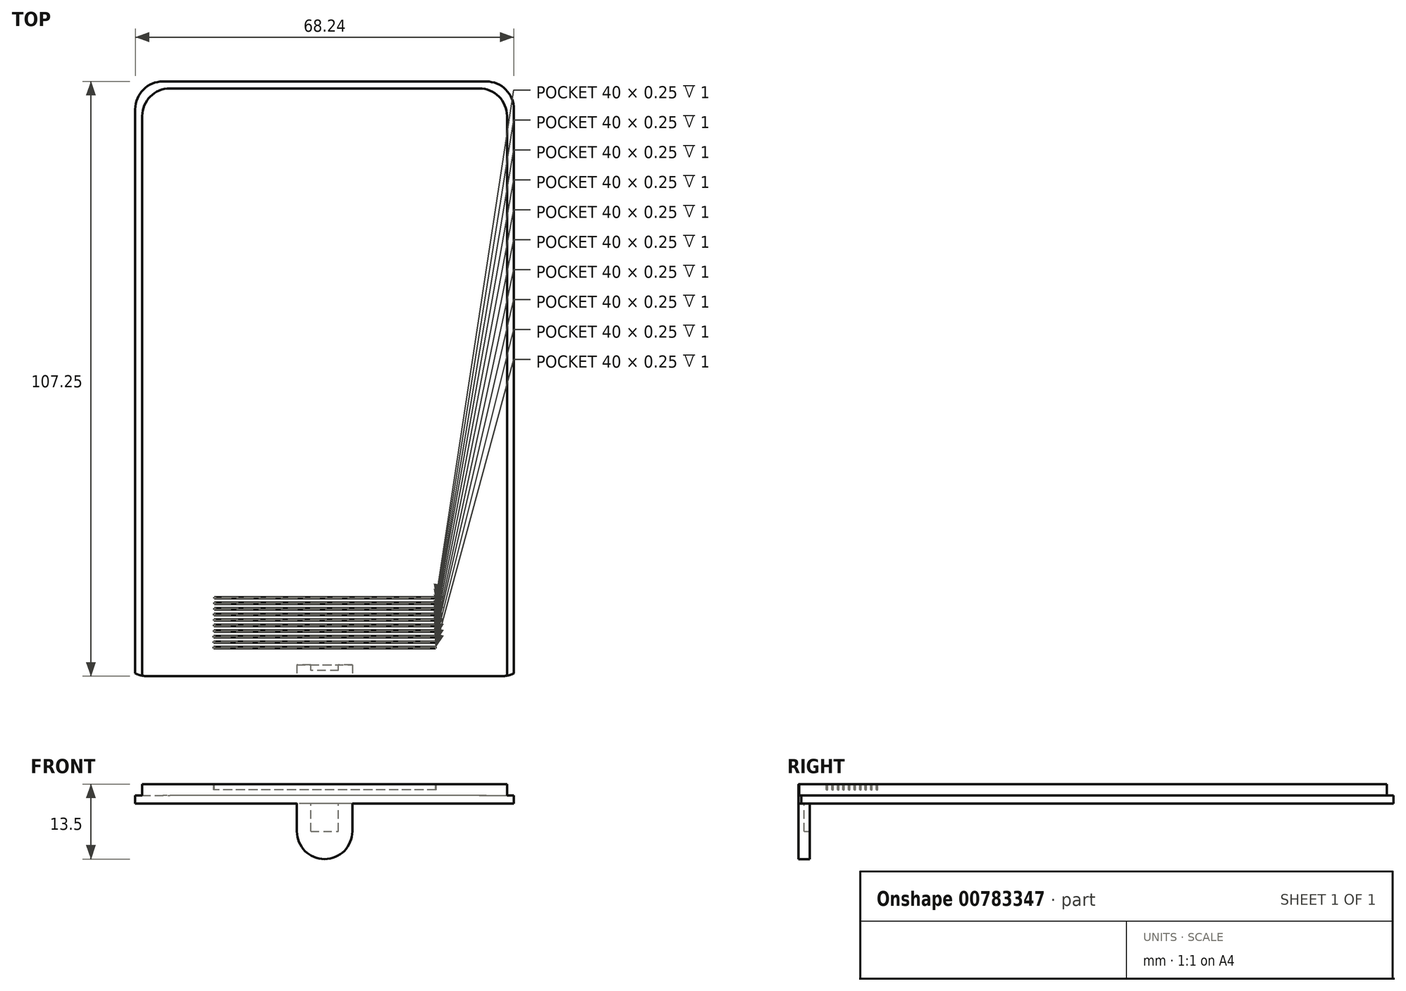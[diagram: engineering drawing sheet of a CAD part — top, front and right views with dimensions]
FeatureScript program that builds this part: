
annotation { "Feature Type Name" : "Feature", "Feature Type Description" : "" }
export const myFeature = defineFeature(function(context is Context, id is Id, definition is map)
    precondition{}
    {
        {
            var Q0;
            Q0=qCreatedBy(makeId("Front.planeOp"),FACE);
            var sketch = newSketch(context, id + "F0", { "sketchPlane" : qUnion([Q0])});
            skLineSegment(sketch, "E0.top", {"start": v(32.88, 3.5) * mm, "end": v(-32.87, 3.5) * mm});
            skLineSegment(sketch, "E0.left", {"start": v(32.88, 1.5) * mm, "end": v(32.88, 3.5) * mm});
            skLineSegment(sketch, "E0.right", {"start": v(-32.87, 1.5) * mm, "end": v(-32.87, 3.5) * mm});
            skLineSegment(sketch, "E1.bottom", {"start": v(34.12, 0) * mm, "end": v(-34.12, 0) * mm});
            skLineSegment(sketch, "E1.left", {"start": v(34.13, 0) * mm, "end": v(34.13, 1.5) * mm});
            skLineSegment(sketch, "E1.right", {"start": v(-34.12, 0) * mm, "end": v(-34.12, 1.5) * mm});
            skLineSegment(sketch, "E2", {"start": v(0, 3.25) * mm, "end": v(0, 44.31) * mm, "construction": true});
            skLineSegment(sketch, "E3", {"start": v(-34.12, 1.5) * mm, "end": v(-32.87, 1.5) * mm});
            skLineSegment(sketch, "E4", {"start": v(32.88, 1.5) * mm, "end": v(34.13, 1.5) * mm});
            skSolve(sketch);
        }
        {
            var Q0;
            Q0=makeQuery(id+"F0.imprint","IMPRINT",FACE,{"disambiguationData":[TD([[makeQuery(id+"F0.imprint","IMPRINT",EDGE,{"derivedFrom":sQuery(id+"F0.wireOp",EDGE,"E0.top")}),1.0]])]});
            extrude(context, id + "F1", {"entities" : qUnion([Q0]), "oppositeDirection" : true, "depth" : 106 * mm, "offsetDistance" : 25 * mm});
        }
        {
            var Q0;
            Q0=makeQuery(id+"F1.opExtrude","CAP_FACE",FACE,{"disambiguationData":[OSD([sQuery(id+"F0.wireOp",EDGE,"E0.top"),sQuery(id+"F0.wireOp",EDGE,"E0.left"),sQuery(id+"F0.wireOp",EDGE,"E0.right"),sQuery(id+"F0.wireOp",EDGE,"E1.bottom"),sQuery(id+"F0.wireOp",EDGE,"E1.left"),sQuery(id+"F0.wireOp",EDGE,"E1.right"),sQuery(id+"F0.wireOp",EDGE,"E3"),sQuery(id+"F0.wireOp",EDGE,"E4")])],"isStart":false});
            var sketch = newSketch(context, id + "F2", { "sketchPlane" : qUnion([Q0])});
            skLineSegment(sketch, "E5.bottom", {"start": v(-34.13, 1.5) * mm, "end": v(34.12, 1.5) * mm});
            skLineSegment(sketch, "E5.top", {"start": v(-34.13, 0) * mm, "end": v(34.12, 0) * mm});
            skLineSegment(sketch, "E5.left", {"start": v(-34.13, 1.5) * mm, "end": v(-34.13, 0) * mm});
            skLineSegment(sketch, "E5.right", {"start": v(34.12, 1.5) * mm, "end": v(34.12, 0) * mm});
            skSolve(sketch);
        }
        {
            var Q0;
            Q0 = qSketchRegion(id + "F2", true);
            extrude(context, id + "F3", {"entities" : qUnion([Q0]), "operationType" : NewBodyOperationType.ADD, "depth" : 1.25 * mm, "offsetDistance" : 25 * mm});
        }
        {
            var Q0;
            Q0=makeQuery(id+"F3.opExtrude","CAP_EDGE",EDGE,{"disambiguationData":[OSD([sQuery(id+"F2.wireOp",EDGE,"E5.left")])],"isStart":false});
            var Q1;
            Q1=makeQuery(id+"F3.opExtrude","CAP_EDGE",EDGE,{"disambiguationData":[OSD([sQuery(id+"F2.wireOp",EDGE,"E5.right")])],"isStart":false});
            var Q2;
            Q2=makeQuery(id+"F1.opExtrude","CAP_EDGE",EDGE,{"disambiguationData":[OSD([sQuery(id+"F0.wireOp",EDGE,"E0.right")])],"isStart":false});
            var Q3;
            Q3=makeQuery(id+"F1.opExtrude","CAP_EDGE",EDGE,{"disambiguationData":[OSD([sQuery(id+"F0.wireOp",EDGE,"E0.left")])],"isStart":false});
            fillet(context, id + "F4", {"entities" : qUnion([Q0, Q1, Q2, Q3]), "radius" : 5 * mm, "tangentPropagation" : true, "allowEdgeOverflow" : false});
        }
        {
            var Q0;
            Q0=qCreatedBy(makeId("Top.planeOp"),FACE);
            var sketch = newSketch(context, id + "F5", { "sketchPlane" : qUnion([Q0])});
            skLineSegment(sketch, "E6.0.0", {"start": v(-34.12, 73) * mm, "end": v(34.12, 73) * mm, "construction": true});
            skLineSegment(sketch, "E6.0.1", {"start": v(34.12, 73) * mm, "end": v(34.12, 5) * mm, "construction": true});
            skLineSegment(sketch, "E6.0.2", {"start": v(29.12, 0) * mm, "end": v(-29.12, 0) * mm, "construction": true});
            skLineSegment(sketch, "E6.0.3", {"start": v(-34.12, 5) * mm, "end": v(-34.12, 73) * mm, "construction": true});
            skPoint(sketch, "E7.middle", {"position": v(-2.88, 36.5) * mm});
            skPoint(sketch, "E8.visualSharp", {"position": v(-37, 0) * mm});
            skArc(sketch, "E8.filletArc", {"start": v(-37, 5) * mm, "mid": v(-35.54, 1.46) * mm, "end": v(-32, 0) * mm, "construction": true});
            skPoint(sketch, "E9.visualSharp", {"position": v(37, 0) * mm});
            skArc(sketch, "E9.filletArc", {"start": v(32, 0) * mm, "mid": v(35.54, 1.46) * mm, "end": v(37, 5) * mm, "construction": true});
            skArc(sketch, "E10", {"start": v(-37, 5) * mm, "mid": v(-35.54, 1.46) * mm, "end": v(-32, 0) * mm});
            skLineSegment(sketch, "E11", {"start": v(-32.48, -8.24) * mm, "end": v(-32, 0) * mm});
            skLineSegment(sketch, "E12", {"start": v(-37, 5) * mm, "end": v(-47.45, 5.13) * mm});
            skLineSegment(sketch, "E13", {"start": v(0, 0) * mm, "end": v(0, 9.43) * mm, "construction": true});
            skLineSegment(sketch, "E14.MirrorCS", {"start": v(37, 5) * mm, "end": v(47.87, 4.85) * mm});
            skLineSegment(sketch, "E15.MirrorCS", {"start": v(31.7, -9.05) * mm, "end": v(32, 0) * mm});
            skPoint(sketch, "E16.MirrorP", {"position": v(31.25, 0) * mm});
            skLineSegment(sketch, "E17", {"start": v(-47.45, 5.13) * mm, "end": v(-32.48, -8.24) * mm});
            skLineSegment(sketch, "E18", {"start": v(31.7, -9.05) * mm, "end": v(47.87, 4.85) * mm});
            skArc(sketch, "E19.MirrorCS", {"start": v(37, 5) * mm, "mid": v(35.54, 1.46) * mm, "end": v(32, 0) * mm});
            skArc(sketch, "E20.MirrorCS", {"start": v(37, 5) * mm, "mid": v(35.54, 1.46) * mm, "end": v(32, 0) * mm, "construction": true});
            skSolve(sketch);
        }
        {
            var Q0;
            Q0 = qSketchRegion(id + "F5", true);
            extrude(context, id + "F6", {"entities" : qUnion([Q0]), "operationType" : NewBodyOperationType.REMOVE, "depth" : 25 * mm, "offsetDistance" : 25 * mm});
        }
        {
            var Q0;
            Q0=makeQuery(id+"F1.opExtrude","CAP_FACE",FACE,{"disambiguationData":[OSD([sQuery(id+"F0.wireOp",EDGE,"E0.top"),sQuery(id+"F0.wireOp",EDGE,"E0.left"),sQuery(id+"F0.wireOp",EDGE,"E0.right"),sQuery(id+"F0.wireOp",EDGE,"E1.bottom"),sQuery(id+"F0.wireOp",EDGE,"E1.left"),sQuery(id+"F0.wireOp",EDGE,"E1.right"),sQuery(id+"F0.wireOp",EDGE,"E3"),sQuery(id+"F0.wireOp",EDGE,"E4")])],"isStart":true});
            var sketch = newSketch(context, id + "F7", { "sketchPlane" : qUnion([Q0])});
            skLineSegment(sketch, "E21.bottom", {"start": v(5, -10) * mm, "end": v(-5, -10) * mm});
            skLineSegment(sketch, "E21.top", {"start": v(5, 0) * mm, "end": v(-5, 0) * mm});
            skLineSegment(sketch, "E21.left", {"start": v(5, -10) * mm, "end": v(5, 0) * mm});
            skLineSegment(sketch, "E21.right", {"start": v(-5, -10) * mm, "end": v(-5, 0) * mm});
            skPoint(sketch, "E21.middle", {"position": v(0, -5) * mm});
            skSolve(sketch);
        }
        {
            var Q0;
            Q0 = qSketchRegion(id + "F7", true);
            extrude(context, id + "F8", {"entities" : qUnion([Q0]), "operationType" : NewBodyOperationType.ADD, "oppositeDirection" : true, "depth" : 2 * mm, "offsetDistance" : 25 * mm});
        }
        {
            var Q0;
            Q0=makeQuery(id+"F8.opExtrude","SWEPT_EDGE",EDGE,{"disambiguationData":[OSD([sQuery(id+"F0.wireOp",EDGE,"E1.bottom"),sQuery(id+"F7.wireOp",EDGE,"E21.top"),sQuery(id+"F7.wireOp",EDGE,"E21.left")])]});
            var Q1;
            Q1=makeQuery(id+"F8.opExtrude","SWEPT_EDGE",EDGE,{"disambiguationData":[OSD([sQuery(id+"F0.wireOp",EDGE,"E1.bottom"),sQuery(id+"F7.wireOp",EDGE,"E21.top"),sQuery(id+"F7.wireOp",EDGE,"E21.right")])]});
            var Q2;
            Q2=makeQuery(id+"F8.opExtrude","SWEPT_EDGE",EDGE,{"disambiguationData":[OSD([sQuery(id+"F7.wireOp",EDGE,"E21.bottom"),sQuery(id+"F7.wireOp",EDGE,"E21.right")])]});
            var Q3;
            Q3=makeQuery(id+"F8.opExtrude","SWEPT_EDGE",EDGE,{"disambiguationData":[OSD([sQuery(id+"F7.wireOp",EDGE,"E21.bottom"),sQuery(id+"F7.wireOp",EDGE,"E21.left")])]});
            fillet(context, id + "F9", {"entities" : qUnion([Q0, Q1, Q2, Q3]), "radius" : 5 * mm, "tangentPropagation" : true, "allowEdgeOverflow" : false});
        }
        {
            var Q0;
            Q0=makeQuery(id+"F8.opExtrude","CAP_FACE",FACE,{"disambiguationData":[OSD([sQuery(id+"F7.wireOp",EDGE,"E21.bottom"),sQuery(id+"F7.wireOp",EDGE,"E21.top"),sQuery(id+"F7.wireOp",EDGE,"E21.left"),sQuery(id+"F7.wireOp",EDGE,"E21.right")])],"isStart":false});
            var sketch = newSketch(context, id + "F10", { "sketchPlane" : qUnion([Q0])});
            skLineSegment(sketch, "E22.bottom", {"start": v(2.5, -5) * mm, "end": v(-2.5, -5) * mm});
            skLineSegment(sketch, "E22.top", {"start": v(2.5, 0) * mm, "end": v(-2.5, 0) * mm});
            skLineSegment(sketch, "E22.left", {"start": v(2.5, -5) * mm, "end": v(2.5, 0) * mm});
            skLineSegment(sketch, "E22.right", {"start": v(-2.5, -5) * mm, "end": v(-2.5, 0) * mm});
            skPoint(sketch, "E22.middle", {"position": v(0, -2.5) * mm});
            skPoint(sketch, "E23", {"position": v(0, 0) * mm});
            skSolve(sketch);
        }
        {
            var Q0;
            Q0 = qSketchRegion(id + "F10", true);
            extrude(context, id + "F11", {"entities" : qUnion([Q0]), "operationType" : NewBodyOperationType.REMOVE, "oppositeDirection" : true, "depth" : 1 * mm, "offsetDistance" : 25 * mm});
        }
        {
            var Q0;
            Q0=makeQuery(id+"F1.opExtrude","SWEPT_FACE",FACE,{"disambiguationData":[OSD([sQuery(id+"F0.wireOp",EDGE,"E0.top")])]});
            var sketch = newSketch(context, id + "F12", { "sketchPlane" : qUnion([Q0])});
            skLineSegment(sketch, "E24.bottom", {"start": v(20, 5) * mm, "end": v(-20, 5) * mm});
            skLineSegment(sketch, "E24.top", {"start": v(20, 5.25) * mm, "end": v(-20, 5.25) * mm});
            skLineSegment(sketch, "E24.left", {"start": v(20, 5) * mm, "end": v(20, 5.25) * mm});
            skLineSegment(sketch, "E24.right", {"start": v(-20, 5) * mm, "end": v(-20, 5.25) * mm});
            skPoint(sketch, "E24.middle", {"position": v(0, 5.13) * mm});
            skLineSegment(sketch, "E25", {"start": v(0, 0) * mm, "end": v(0, 5) * mm, "construction": true});
            skPoint(sketch, "E26.0.1.0", {"position": v(0.02, 6.12) * mm});
            skLineSegment(sketch, "E26.0.1.1", {"start": v(20.02, 6.25) * mm, "end": v(-19.98, 6.25) * mm});
            skLineSegment(sketch, "E26.0.1.2", {"start": v(20.02, 6) * mm, "end": v(-19.98, 6) * mm});
            skLineSegment(sketch, "E26.0.1.3", {"start": v(20.02, 6) * mm, "end": v(20.02, 6.25) * mm});
            skLineSegment(sketch, "E26.0.1.4", {"start": v(-19.98, 6) * mm, "end": v(-19.98, 6.25) * mm});
            skPoint(sketch, "E26.0.2.0", {"position": v(0.03, 7.12) * mm});
            skLineSegment(sketch, "E26.0.2.1", {"start": v(20.03, 7.25) * mm, "end": v(-19.97, 7.25) * mm});
            skLineSegment(sketch, "E26.0.2.2", {"start": v(20.03, 7) * mm, "end": v(-19.97, 7) * mm});
            skLineSegment(sketch, "E26.0.2.3", {"start": v(20.03, 7) * mm, "end": v(20.03, 7.25) * mm});
            skLineSegment(sketch, "E26.0.2.4", {"start": v(-19.97, 7) * mm, "end": v(-19.97, 7.25) * mm});
            skPoint(sketch, "E26.0.3.0", {"position": v(0.05, 8.12) * mm});
            skLineSegment(sketch, "E26.0.3.1", {"start": v(20.05, 8.25) * mm, "end": v(-19.95, 8.25) * mm});
            skLineSegment(sketch, "E26.0.3.2", {"start": v(20.05, 8) * mm, "end": v(-19.95, 8) * mm});
            skLineSegment(sketch, "E26.0.3.3", {"start": v(20.05, 8) * mm, "end": v(20.05, 8.25) * mm});
            skLineSegment(sketch, "E26.0.3.4", {"start": v(-19.95, 8) * mm, "end": v(-19.95, 8.25) * mm});
            skPoint(sketch, "E26.0.4.0", {"position": v(0.07, 9.12) * mm});
            skLineSegment(sketch, "E26.0.4.1", {"start": v(20.07, 9.25) * mm, "end": v(-19.93, 9.25) * mm});
            skLineSegment(sketch, "E26.0.4.2", {"start": v(20.07, 9) * mm, "end": v(-19.93, 9) * mm});
            skLineSegment(sketch, "E26.0.4.3", {"start": v(20.07, 9) * mm, "end": v(20.07, 9.25) * mm});
            skLineSegment(sketch, "E26.0.4.4", {"start": v(-19.93, 9) * mm, "end": v(-19.93, 9.25) * mm});
            skPoint(sketch, "E26.0.5.0", {"position": v(0.08, 10.12) * mm});
            skLineSegment(sketch, "E26.0.5.1", {"start": v(20.08, 10.25) * mm, "end": v(-19.92, 10.25) * mm});
            skLineSegment(sketch, "E26.0.5.2", {"start": v(20.08, 10) * mm, "end": v(-19.92, 10) * mm});
            skLineSegment(sketch, "E26.0.5.3", {"start": v(20.08, 10) * mm, "end": v(20.08, 10.25) * mm});
            skLineSegment(sketch, "E26.0.5.4", {"start": v(-19.92, 10) * mm, "end": v(-19.92, 10.25) * mm});
            skPoint(sketch, "E26.0.6.0", {"position": v(0.1, 11.12) * mm});
            skLineSegment(sketch, "E26.0.6.1", {"start": v(20.1, 11.25) * mm, "end": v(-19.9, 11.25) * mm});
            skLineSegment(sketch, "E26.0.6.2", {"start": v(20.1, 11) * mm, "end": v(-19.9, 11) * mm});
            skLineSegment(sketch, "E26.0.6.3", {"start": v(20.1, 11) * mm, "end": v(20.1, 11.25) * mm});
            skLineSegment(sketch, "E26.0.6.4", {"start": v(-19.9, 11) * mm, "end": v(-19.9, 11.25) * mm});
            skPoint(sketch, "E26.0.7.0", {"position": v(0.12, 12.12) * mm});
            skLineSegment(sketch, "E26.0.7.1", {"start": v(20.12, 12.25) * mm, "end": v(-19.88, 12.25) * mm});
            skLineSegment(sketch, "E26.0.7.2", {"start": v(20.12, 12) * mm, "end": v(-19.88, 12) * mm});
            skLineSegment(sketch, "E26.0.7.3", {"start": v(20.12, 12) * mm, "end": v(20.12, 12.25) * mm});
            skLineSegment(sketch, "E26.0.7.4", {"start": v(-19.88, 12) * mm, "end": v(-19.88, 12.25) * mm});
            skPoint(sketch, "E26.0.8.0", {"position": v(0.14, 13.12) * mm});
            skLineSegment(sketch, "E26.0.8.1", {"start": v(20.14, 13.25) * mm, "end": v(-19.86, 13.25) * mm});
            skLineSegment(sketch, "E26.0.8.2", {"start": v(20.14, 13) * mm, "end": v(-19.86, 13) * mm});
            skLineSegment(sketch, "E26.0.8.3", {"start": v(20.14, 13) * mm, "end": v(20.14, 13.25) * mm});
            skLineSegment(sketch, "E26.0.8.4", {"start": v(-19.86, 13) * mm, "end": v(-19.86, 13.25) * mm});
            skPoint(sketch, "E26.0.9.0", {"position": v(0.15, 14.12) * mm});
            skLineSegment(sketch, "E26.0.9.1", {"start": v(20.15, 14.25) * mm, "end": v(-19.85, 14.25) * mm});
            skLineSegment(sketch, "E26.0.9.2", {"start": v(20.15, 14) * mm, "end": v(-19.85, 14) * mm});
            skLineSegment(sketch, "E26.0.9.3", {"start": v(20.15, 14) * mm, "end": v(20.15, 14.25) * mm});
            skLineSegment(sketch, "E26.0.9.4", {"start": v(-19.85, 14) * mm, "end": v(-19.85, 14.25) * mm});
            skLineSegment(sketch, "E26.direction1", {"start": v(-20, 5) * mm, "end": v(5, 5) * mm, "construction": true});
            skLineSegment(sketch, "E26.direction2", {"start": v(-20, 5) * mm, "end": v(-19.98, 6) * mm, "construction": true});
            skSolve(sketch);
        }
        {
            var Q0;
            Q0 = qSketchRegion(id + "F12", true);
            extrude(context, id + "F13", {"entities" : qUnion([Q0]), "operationType" : NewBodyOperationType.REMOVE, "oppositeDirection" : true, "depth" : 1 * mm, "offsetDistance" : 25 * mm});
        }
    });
